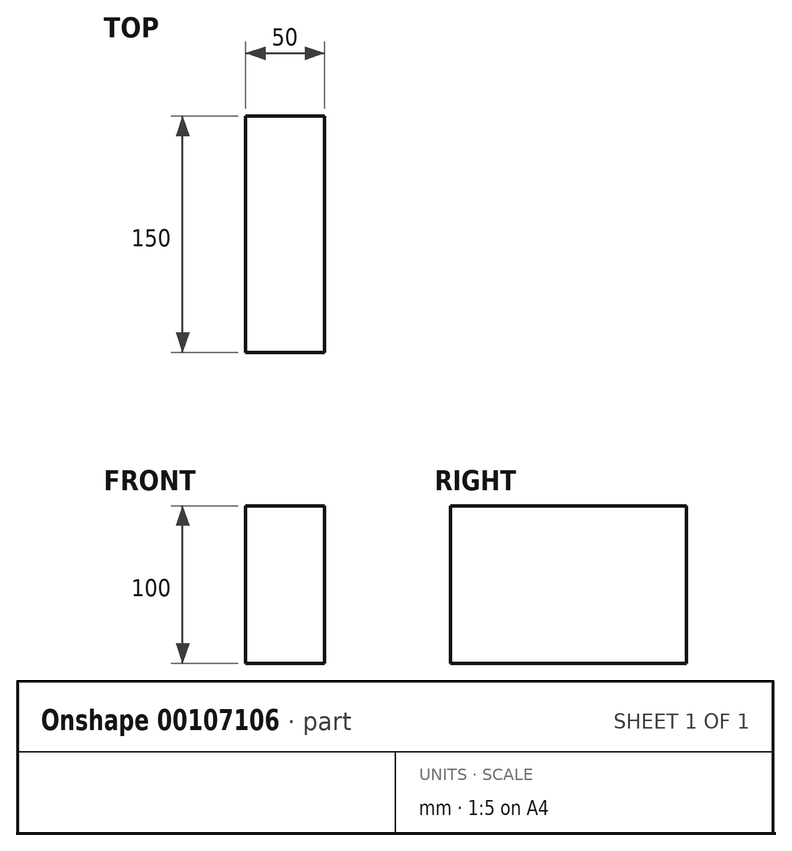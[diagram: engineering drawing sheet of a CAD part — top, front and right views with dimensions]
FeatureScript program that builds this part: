
annotation { "Feature Type Name" : "Feature", "Feature Type Description" : "" }
export const myFeature = defineFeature(function(context is Context, id is Id, definition is map)
    precondition{}
    {
        {
            var Q0;
            Q0=qCreatedBy(makeId("Front.planeOp"),FACE);
            var sketch = newSketch(context, id + "F0", { "sketchPlane" : qUnion([Q0])});
            skLineSegment(sketch, "E0.bottom", {"start": v(0, 0) * mm, "end": v(50, 0) * mm});
            skLineSegment(sketch, "E0.top", {"start": v(0, 100) * mm, "end": v(50, 100) * mm});
            skLineSegment(sketch, "E0.left", {"start": v(0, 0) * mm, "end": v(0, 100) * mm});
            skLineSegment(sketch, "E0.right", {"start": v(50, 0) * mm, "end": v(50, 100) * mm});
            skSolve(sketch);
        }
        {
            var Q0;
            Q0=qSketchRegion(id+"F0",true);
            extrude(context, id + "F1", {"entities" : qUnion([Q0]), "depth" : 150 * mm});
        }
    });
